# Revit family: Galaxy-Metal-Doors_Single
name_source: partatom
category: Doors
units: mm (PartAtom-declared; Revit-internal decimal feet)

## family parameters
Always vertical = Yes
Classification Number = 23.30.10.14.11
Cut with Voids When Loaded = No
Host = Wall
Room Calculation Point = No
Shared = No

## types (1)
- ByType
    ADA Compliant = Yes
    Assembly Code = B2030220
    Back Rabbet Depth = 0' - 1 15/16"
    Construction Details = http://www.arcat.com
    Description = Galaxy Steel Door as Specified
    Door Glazing = Glass - Clear - Galaxy - Tempered
    Expected Lifespan (Years) = 0
    Fire Rating = As Specified in 08110
    Frame Finish = Metal - Steel - Galaxy - Primed
    Frame Thickness = 0' - 3 1/2"
    Frame Width = 0' - 2"
    Function = Interior
    Green Building-LEED = http://www.arcat.com
    Hardware Finish = Metal - Stainless Steel - Galaxy - Brushed
    Height = 7' - 0"
    Keynote = 08 11 10
    Maintenance Schedule (Months) = 0
    Manufacturer = Galaxy Metal Products, LLC
    Manufacturer Website = http://galaxymetalproducts.com
    Model = As Specified
    Panel Height = 7' - 0"
    Panel Material = Metal - Steel - Galaxy - Primed
    Panel Width = 3' - 0"
    Product Data = http://www.arcat.com
    RO Offset = 0' - 0"
    R_Value = 0
    Rough Height = 7' - 0"
    Rough Width = 3' - 0"
    Sales Information = http://www.arcat.com
    Send Message = http://www.arcat.com
    Sound Transmission Class (STC) = 0
    Specification = http://www.arcat.com
    Stop Depth = 0' - 0 5/8"
    Thickness = 0' - 1 3/4"
    URL = galaxymetalproducts.com
    Wall Closure = By host
    Warranty Duration (Years) = 0
    Width = 3' - 0"

## geometry (parser evidence)
native form markers: Blend x2, Sweep x11
no freeform markers — native parametric forms only
